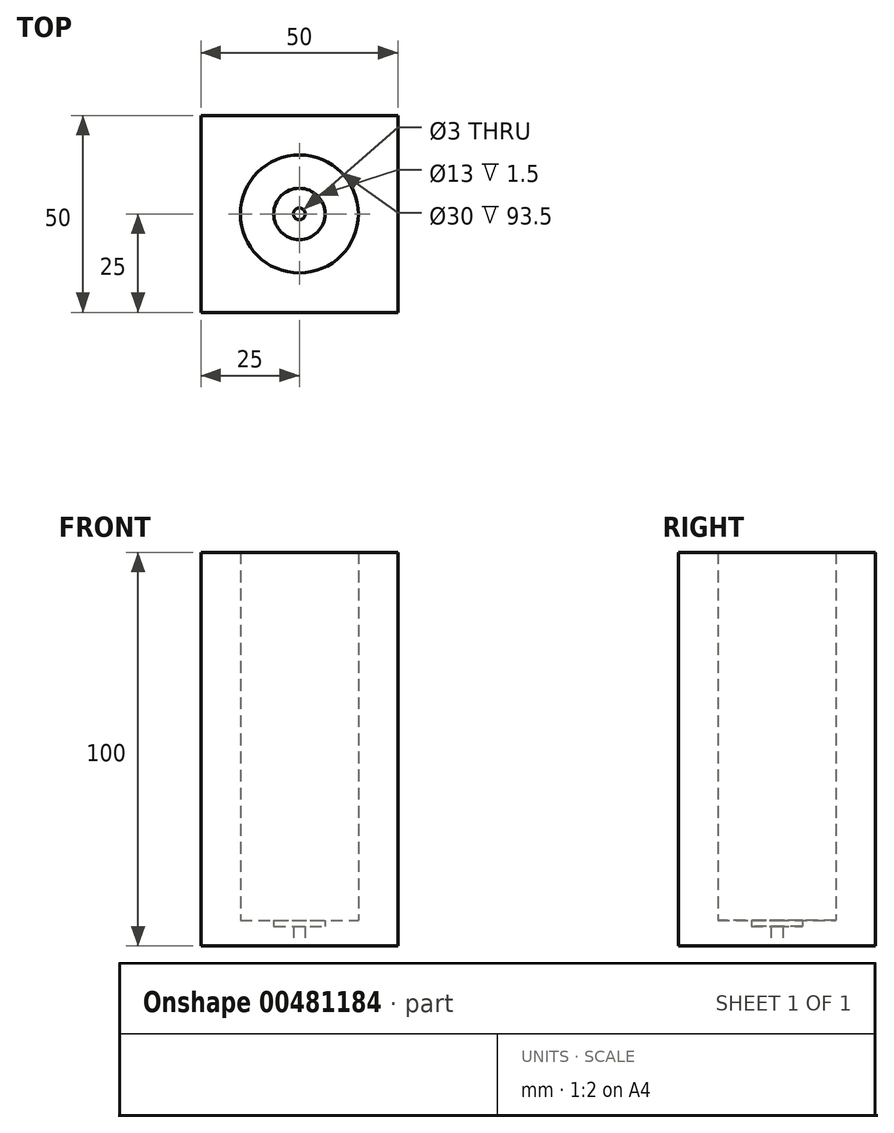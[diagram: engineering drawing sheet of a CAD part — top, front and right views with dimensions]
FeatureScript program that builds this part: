
annotation { "Feature Type Name" : "Feature", "Feature Type Description" : "" }
export const myFeature = defineFeature(function(context is Context, id is Id, definition is map)
    precondition{}
    {
        {
            var Q0;
            Q0=qCreatedBy(makeId("Top.planeOp"),FACE);
            var sketch = newSketch(context, id + "F0", { "sketchPlane" : qUnion([Q0])});
            skLineSegment(sketch, "E0.bottom", {"start": v(25, 25) * mm, "end": v(-25, 25) * mm});
            skLineSegment(sketch, "E0.top", {"start": v(25, -25) * mm, "end": v(-25, -25) * mm});
            skLineSegment(sketch, "E0.left", {"start": v(25, 25) * mm, "end": v(25, -25) * mm});
            skLineSegment(sketch, "E0.right", {"start": v(-25, 25) * mm, "end": v(-25, -25) * mm});
            skPoint(sketch, "E0.middle", {"position": v(0, 0) * mm});
            skSolve(sketch);
        }
        {
            var Q0;
            Q0 = qSketchRegion(id + "F0", true);
            extrude(context, id + "F1", {"entities" : qUnion([Q0]), "depth" : 100 * mm});
        }
        {
            var Q0;
            Q0=qCreatedBy(makeId("Front.planeOp"),FACE);
            var sketch = newSketch(context, id + "F2", { "sketchPlane" : qUnion([Q0])});
            skLineSegment(sketch, "E1", {"start": v(1.5, 0) * mm, "end": v(1.5, 5) * mm});
            skLineSegment(sketch, "E2", {"start": v(1.5, 5) * mm, "end": v(6.5, 5) * mm});
            skLineSegment(sketch, "E3", {"start": v(6.5, 5) * mm, "end": v(6.5, 6.5) * mm});
            skLineSegment(sketch, "E4", {"start": v(6.5, 6.5) * mm, "end": v(15, 6.5) * mm});
            skLineSegment(sketch, "E5", {"start": v(15, 6.5) * mm, "end": v(15, 100) * mm});
            skLineSegment(sketch, "E6", {"start": v(0, 100) * mm, "end": v(15, 100) * mm});
            skLineSegment(sketch, "E7", {"start": v(0, 100) * mm, "end": v(0, 0) * mm});
            skLineSegment(sketch, "E8", {"start": v(1.5, 0) * mm, "end": v(0, 0) * mm});
            skSolve(sketch);
        }
        {
            var Q0;
            Q0 = qSketchRegion(id + "F2", true);
            var Q1;
            Q1=sQuery(id+"F2.wireOp",EDGE,"E7");
            revolve(context, id + "F3", {"operationType" : NewBodyOperationType.REMOVE, "entities" : qUnion([Q0]), "axis" : qUnion([Q1]), "revolveType" : RevolveType.FULL, "oppositeDirection" : true});
        }
    });
